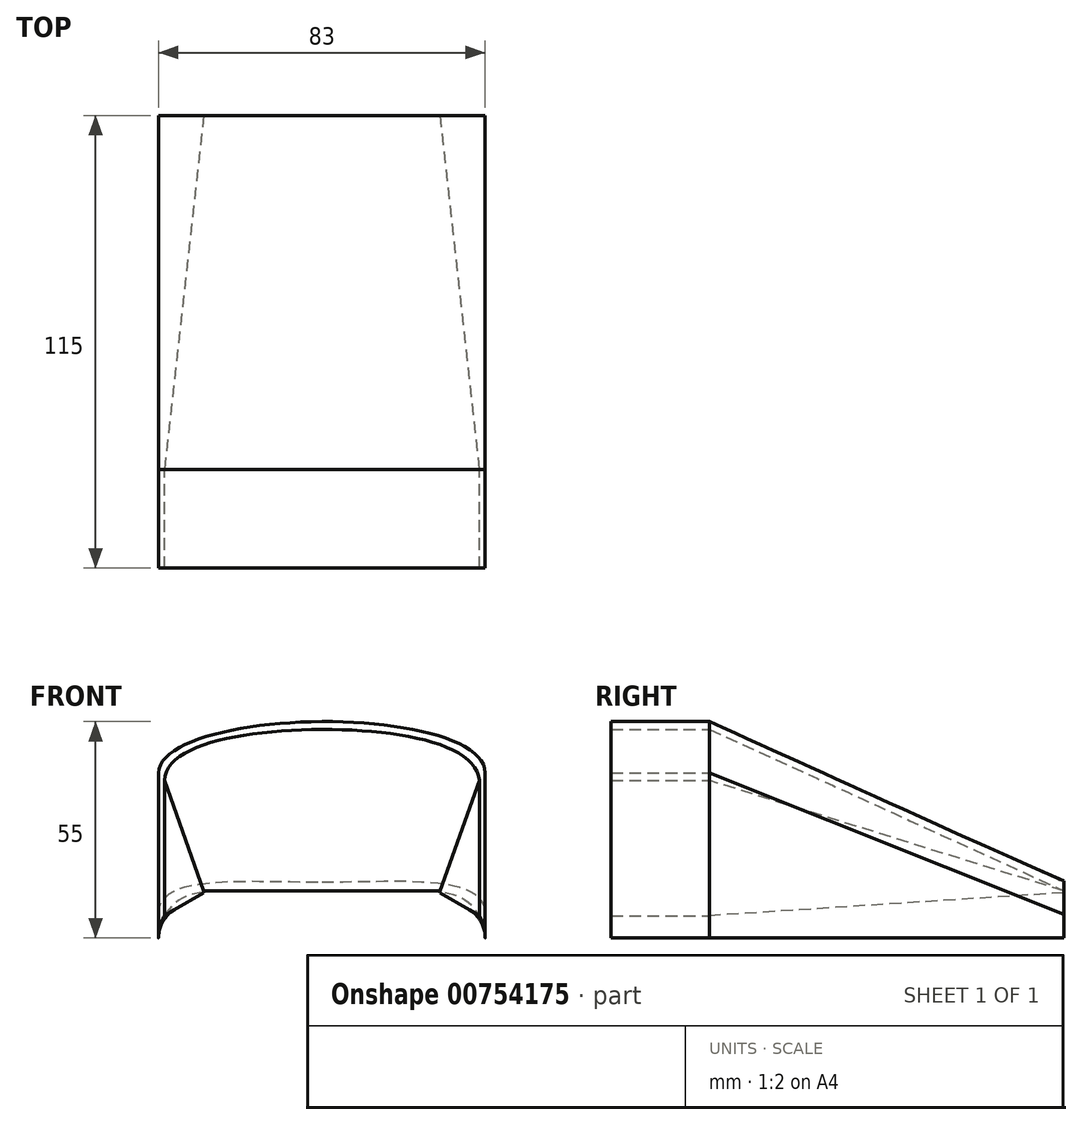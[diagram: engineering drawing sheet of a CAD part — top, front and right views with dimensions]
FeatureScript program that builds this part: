
annotation { "Feature Type Name" : "Feature", "Feature Type Description" : "" }
export const myFeature = defineFeature(function(context is Context, id is Id, definition is map)
    precondition{}
    {
        {
            var Q0;
            Q0=qCreatedBy(makeId("Front.planeOp"),FACE);
            var sketch = newSketch(context, id + "F0", { "sketchPlane" : qUnion([Q0])});
            skLineSegment(sketch, "E0.bottom", {"start": v(-30, 20) * mm, "end": v(30, 20) * mm});
            skLineSegment(sketch, "E0.top", {"start": v(-30, -20) * mm, "end": v(30, -20) * mm});
            skLineSegment(sketch, "E0.left", {"start": v(-40, 10) * mm, "end": v(-40, -10) * mm});
            skLineSegment(sketch, "E0.right", {"start": v(40, 10) * mm, "end": v(40, -10) * mm});
            skPoint(sketch, "E0.middle", {"position": v(0, 0) * mm});
            skPoint(sketch, "E1.visualSharp", {"position": v(-40, 20) * mm});
            skArc(sketch, "E1.filletArc", {"start": v(-30, 20) * mm, "mid": v(-37.07, 17.07) * mm, "end": v(-40, 10) * mm});
            skPoint(sketch, "E2.visualSharp", {"position": v(40, 20) * mm});
            skArc(sketch, "E2.filletArc", {"start": v(40, 10) * mm, "mid": v(37.07, 17.07) * mm, "end": v(30, 20) * mm});
            skPoint(sketch, "E3.visualSharp", {"position": v(-40, -20) * mm});
            skArc(sketch, "E3.filletArc", {"start": v(-40, -10) * mm, "mid": v(-37.07, -17.07) * mm, "end": v(-30, -20) * mm});
            skPoint(sketch, "E4.visualSharp", {"position": v(40, -20) * mm});
            skArc(sketch, "E4.filletArc", {"start": v(30, -20) * mm, "mid": v(37.07, -17.07) * mm, "end": v(40, -10) * mm});
            skLineSegment(sketch, "E5.0", {"start": v(-30, -21.5) * mm, "end": v(30, -21.5) * mm});
            skArc(sketch, "E5.1", {"start": v(-41.5, -10) * mm, "mid": v(-38.13, -18.13) * mm, "end": v(-30, -21.5) * mm});
            skArc(sketch, "E5.2", {"start": v(30, -21.5) * mm, "mid": v(38.13, -18.13) * mm, "end": v(41.5, -10) * mm});
            skLineSegment(sketch, "E5.3", {"start": v(-41.5, 10) * mm, "end": v(-41.5, -10) * mm});
            skLineSegment(sketch, "E5.4", {"start": v(41.5, 10) * mm, "end": v(41.5, -10) * mm});
            skArc(sketch, "E5.5", {"start": v(41.5, 10) * mm, "mid": v(38.13, 18.13) * mm, "end": v(30, 21.5) * mm});
            skLineSegment(sketch, "E5.6", {"start": v(-30, 21.5) * mm, "end": v(30, 21.5) * mm});
            skArc(sketch, "E5.7", {"start": v(-30, 21.5) * mm, "mid": v(-38.13, 18.13) * mm, "end": v(-41.5, 10) * mm});
            skLineSegment(sketch, "E6", {"start": v(-30, 21.5) * mm, "end": v(-30, 20) * mm});
            skLineSegment(sketch, "E7", {"start": v(30, 21.5) * mm, "end": v(30, 20) * mm});
            skSolve(sketch);
        }
        {
            var Q0;
            Q0=qCreatedBy(makeId("Front.planeOp"),FACE);
            var sketch = newSketch(context, id + "F1", { "sketchPlane" : qUnion([Q0])});
            skLineSegment(sketch, "E8.bottom", {"start": v(-20, -20) * mm, "end": v(20, -20) * mm});
            skLineSegment(sketch, "E8.top", {"start": v(-20, 20) * mm, "end": v(20, 20) * mm});
            skLineSegment(sketch, "E8.left", {"start": v(-20, -20) * mm, "end": v(-20, 20) * mm});
            skLineSegment(sketch, "E8.right", {"start": v(20, -20) * mm, "end": v(20, 20) * mm});
            skPoint(sketch, "E8.middle", {"position": v(0, 0) * mm});
            skLineSegment(sketch, "E9.bottom", {"start": v(-20, -20) * mm, "end": v(-30, -20) * mm});
            skLineSegment(sketch, "E9.top", {"start": v(-20, 50) * mm, "end": v(-40, 50) * mm});
            skLineSegment(sketch, "E9.left", {"start": v(-20, -20) * mm, "end": v(-20, 50) * mm});
            skLineSegment(sketch, "E9.right", {"start": v(-40, -10) * mm, "end": v(-40, 50) * mm});
            skPoint(sketch, "E10.visualSharp", {"position": v(-40, -20) * mm});
            skArc(sketch, "E10.filletArc", {"start": v(-40, -10) * mm, "mid": v(-37.07, -17.07) * mm, "end": v(-30, -20) * mm});
            skLineSegment(sketch, "E11.bottom", {"start": v(20, -20) * mm, "end": v(30, -20) * mm});
            skLineSegment(sketch, "E11.top", {"start": v(20, 50) * mm, "end": v(40, 50) * mm});
            skLineSegment(sketch, "E11.left", {"start": v(20, -20) * mm, "end": v(20, 50) * mm});
            skLineSegment(sketch, "E11.right", {"start": v(40, -10) * mm, "end": v(40, 50) * mm});
            skPoint(sketch, "E12.visualSharp", {"position": v(40, -20) * mm});
            skArc(sketch, "E12.filletArc", {"start": v(30, -20) * mm, "mid": v(37.07, -17.07) * mm, "end": v(40, -10) * mm});
            skLineSegment(sketch, "E13.0", {"start": v(-41.5, 10) * mm, "end": v(-41.5, -10) * mm});
            skLineSegment(sketch, "E14.0", {"start": v(41.5, 10) * mm, "end": v(41.5, -10) * mm});
            skLineSegment(sketch, "E15", {"start": v(-41.5, 10) * mm, "end": v(-41.5, 52) * mm});
            skLineSegment(sketch, "E16", {"start": v(41.5, 10) * mm, "end": v(41.5, 52) * mm});
            skLineSegment(sketch, "E17", {"start": v(0, 0) * mm, "end": v(0, 65) * mm, "construction": true});
            skFitSpline(sketch, "E18", {"points": [v(-41.5, 52) * mm, v(0, 65) * mm, v(41.5, 52) * mm], "startDerivative": vector(1.44, 48.09) * mm, "endDerivative": vector(0.43, -50.77) * mm});
            skLineSegment(sketch, "E19", {"start": v(0, 65) * mm, "end": v(0, 63) * mm});
            skFitSpline(sketch, "E20", {"points": [v(-40, 50) * mm, v(0, 63) * mm, v(40, 50) * mm], "startDerivative": vector(1.58, 55.12) * mm, "endDerivative": vector(3.87, -56.07) * mm});
            skArc(sketch, "E21.0", {"start": v(-30, 21.5) * mm, "mid": v(-38.13, 18.13) * mm, "end": v(-41.5, 10) * mm});
            skArc(sketch, "E22.0", {"start": v(41.5, 10) * mm, "mid": v(38.13, 18.13) * mm, "end": v(30, 21.5) * mm});
            skSolve(sketch);
        }
        {
            var Q0;
            {var subQ2=sQuery(id+"F1.wireOp",EDGE,"E15");Q0=makeQuery(id+"F1.imprint","IMPRINT",FACE,{"disambiguationData":[TD([[makeQuery(id+"F1.imprint","IMPRINT",EDGE,{"derivedFrom":subQ2}),-1.0]])]});}
            var Q1;
            {var subQ1=sQuery(id+"F1.wireOp",EDGE,"E16");Q1=makeQuery(id+"F1.imprint","IMPRINT",FACE,{"disambiguationData":[TD([[makeQuery(id+"F1.imprint","IMPRINT",EDGE,{"derivedFrom":subQ1}),1.0]])]});}
            extrude(context, id + "F2", {"entities" : qUnion([Q0, Q1]), "depth" : 25 * mm, "offsetDistance" : 25 * mm});
        }
        {
            var Q0;
            Q0=qCreatedBy(makeId("Front.planeOp"),FACE);
            cPlane(context, id + "F3", {"entities" : qUnion([Q0]), "cplaneType" : CPlaneType.OFFSET, "offset" : 90 * mm, "oppositeDirection" : true, "width" : 150 * mm, "height" : 150 * mm});
        }
        {
            var Q0;
            Q0=qCreatedBy(id+"F3.planeOp",FACE);
            var sketch = newSketch(context, id + "F4", { "sketchPlane" : qUnion([Q0])});
            skPoint(sketch, "E23.orphan", {"position": v(41.5, 52) * mm});
            skPoint(sketch, "E24.0.end.orphan", {"position": v(40, 50) * mm});
            skPoint(sketch, "E25.orphan", {"position": v(-41.5, 52) * mm});
            skArc(sketch, "E26.0", {"start": v(41.5, 10) * mm, "mid": v(38.13, 18.13) * mm, "end": v(30, 21.5) * mm});
            skArc(sketch, "E27.0", {"start": v(-30, 21.5) * mm, "mid": v(-38.13, 18.13) * mm, "end": v(-41.5, 10) * mm});
            skLineSegment(sketch, "E28", {"start": v(30, 21.5) * mm, "end": v(30, 22) * mm});
            skLineSegment(sketch, "E29", {"start": v(-30, 21.5) * mm, "end": v(-30, 22) * mm});
            skLineSegment(sketch, "E30", {"start": v(-30, 22) * mm, "end": v(30, 22) * mm});
            skLineSegment(sketch, "E31", {"start": v(41.5, 10) * mm, "end": v(41.5, 16) * mm});
            skLineSegment(sketch, "E32", {"start": v(-41.5, 10) * mm, "end": v(-41.5, 16) * mm});
            skFitSpline(sketch, "E33", {"points": [v(-41.5, 16) * mm, v(0, 24.28) * mm, v(41.5, 16) * mm], "startDerivative": vector(0.15, 62.79) * mm, "endDerivative": vector(0.4, -63.23) * mm});
            skSolve(sketch);
        }
        {
            var Q0;
            Q0=makeQuery(id+"F4.imprint","IMPRINT",FACE,{"disambiguationData":[TD([[makeQuery(id+"F4.imprint","IMPRINT",EDGE,{"derivedFrom":sQuery(id+"F4.wireOp",EDGE,"E26.0")}),-1.0]])]});
            var Q1;
            Q1=makeQuery(id+"F2.opExtrude","CAP_FACE",FACE,{"disambiguationData":[OSD([sQuery(id+"F1.wireOp",EDGE,"E9.right"),sQuery(id+"F1.wireOp",EDGE,"E11.right"),sQuery(id+"F1.wireOp",EDGE,"E15"),sQuery(id+"F1.wireOp",EDGE,"E16"),sQuery(id+"F1.wireOp",EDGE,"E18"),sQuery(id+"F1.wireOp",EDGE,"E20"),sQuery(id+"F1.wireOp",EDGE,"E21.0"),sQuery(id+"F1.wireOp",EDGE,"E22.0")])],"isStart":true});
            loft(context, id + "F5", {"sheetProfilesArray" : [{ "sheetProfileEntities" : qUnion([Q0]) }, { "sheetProfileEntities" : qUnion([Q1]) }]});
        }
    });
